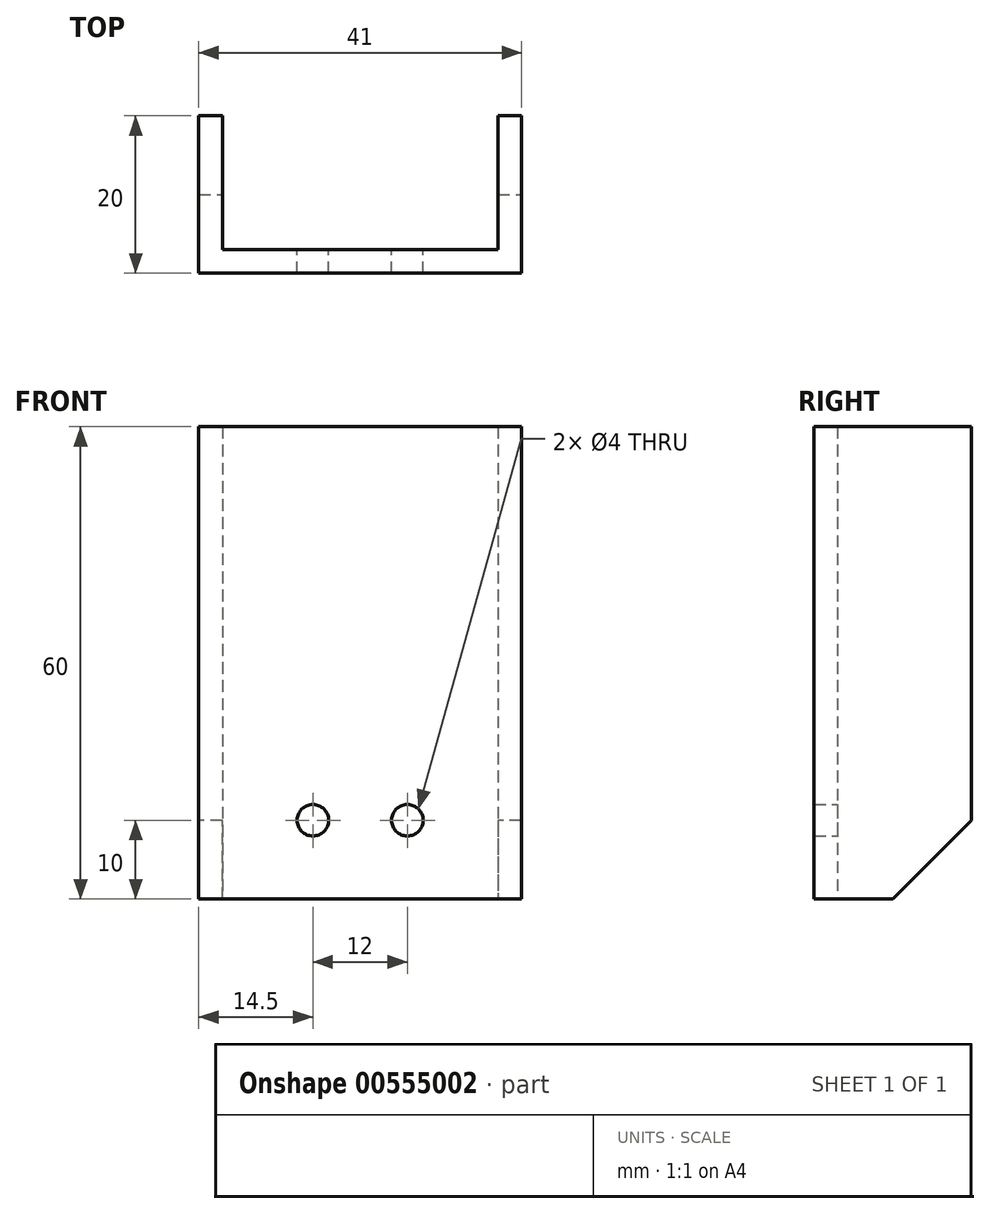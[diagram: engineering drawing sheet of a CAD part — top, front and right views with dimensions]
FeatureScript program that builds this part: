
annotation { "Feature Type Name" : "Feature", "Feature Type Description" : "" }
export const myFeature = defineFeature(function(context is Context, id is Id, definition is map)
    precondition{}
    {
        {
            var Q0;
            Q0=qCreatedBy(makeId("Top.planeOp"),FACE);
            var sketch = newSketch(context, id + "F0", { "sketchPlane" : qUnion([Q0])});
            skLineSegment(sketch, "E0", {"start": v(0, 0) * mm, "end": v(0, 20) * mm});
            skLineSegment(sketch, "E1", {"start": v(0, 20) * mm, "end": v(3, 20) * mm});
            skLineSegment(sketch, "E2", {"start": v(3, 20) * mm, "end": v(3, 3) * mm});
            skLineSegment(sketch, "E3", {"start": v(3, 3) * mm, "end": v(38, 3) * mm});
            skLineSegment(sketch, "E4", {"start": v(38, 3) * mm, "end": v(38, 20) * mm});
            skLineSegment(sketch, "E5", {"start": v(38, 20) * mm, "end": v(41, 20) * mm});
            skLineSegment(sketch, "E6", {"start": v(41, 20) * mm, "end": v(41, 0) * mm});
            skLineSegment(sketch, "E7", {"start": v(41, 0) * mm, "end": v(0, 0) * mm});
            skSolve(sketch);
        }
        {
            var Q0;
            Q0=makeQuery(id+"F0.imprint","IMPRINT",FACE,{"disambiguationData":[TD([[makeQuery(id+"F0.imprint","IMPRINT",EDGE,{"derivedFrom":sQuery(id+"F0.wireOp",EDGE,"E0")}),-1.0]])]});
            extrude(context, id + "F1", {"entities" : qUnion([Q0]), "depth" : 60 * mm, "offsetDistance" : 25 * mm});
        }
        {
            var Q0;
            Q0=makeQuery(id+"F1.opExtrude","CAP_EDGE",EDGE,{"disambiguationData":[OSD([sQuery(id+"F0.wireOp",EDGE,"E5")])],"isStart":true});
            var Q1;
            Q1=makeQuery(id+"F1.opExtrude","CAP_EDGE",EDGE,{"disambiguationData":[OSD([sQuery(id+"F0.wireOp",EDGE,"E1")])],"isStart":true});
            chamfer(context, id + "F2", {"entities" : qUnion([Q0, Q1]), "width" : 10 * mm, "tangentPropagation" : true});
        }
        {
            var Q0;
            Q0=makeQuery(id+"F1.opExtrude","SWEPT_FACE",FACE,{"disambiguationData":[OSD([sQuery(id+"F0.wireOp",EDGE,"E3")])]});
            var sketch = newSketch(context, id + "F3", { "sketchPlane" : qUnion([Q0])});
            skCircle(sketch, "E8", {"center": v(-26.5, 10) * mm, "radius": 2 * mm});
            skCircle(sketch, "E9", {"center": v(-14.5, 10) * mm, "radius": 2 * mm});
            skLineSegment(sketch, "E10", {"start": v(-20.5, 0) * mm, "end": v(-20.5, 26.52) * mm, "construction": true});
            skLineSegment(sketch, "E11", {"start": v(-26.5, 10) * mm, "end": v(-14.5, 10) * mm, "construction": true});
            skPoint(sketch, "E12", {"position": v(-20.5, 10) * mm});
            skSolve(sketch);
        }
        {
            var Q0;
            Q0=makeQuery(id+"F3.imprint","IMPRINT",FACE,{"disambiguationData":[TD([[makeQuery(id+"F3.imprint","IMPRINT",EDGE,{"derivedFrom":sQuery(id+"F3.wireOp",EDGE,"E9")}),1.0]])]});
            var Q1;
            Q1=makeQuery(id+"F3.imprint","IMPRINT",FACE,{"disambiguationData":[TD([[makeQuery(id+"F3.imprint","IMPRINT",EDGE,{"derivedFrom":sQuery(id+"F3.wireOp",EDGE,"E8")}),1.0]])]});
            extrude(context, id + "F4", {"entities" : qUnion([Q0, Q1]), "operationType" : NewBodyOperationType.REMOVE, "oppositeDirection" : true, "depth" : 25 * mm, "offsetDistance" : 25 * mm});
        }
    });
